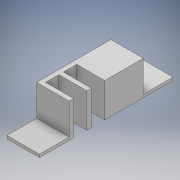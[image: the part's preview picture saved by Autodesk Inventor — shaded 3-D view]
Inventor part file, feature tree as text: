
AUTODESK INVENTOR PART (.ipt)
format: ipt  version: 2017.3 (Build 213256000, 256)  size: 136,704 bytes
history: native  units: mm
features: extrude x3, sketch x3, mirror x1
ambient origin geometry x8: Origin, YZ Plane, XZ Plane, XY Plane, X Axis, Y Axis, Z Axis, Center Point
bodies: Body1 (feature_tree)
feature tree (7):
  extrude  "Extrusion3"  Depth=3.0mm
  extrude  "Extrusion11"  Depth=23.0mm TaperAngle=0.0deg
  mirror  "Mirror1"
  extrude  "Extrusion12"  Depth=2.0mm TaperAngle=0.0deg
  sketch  "Sketch3"  dims[d7=50.0mm d8=3.0mm]
  sketch  "Sketch11"  dims[d9=3.0mm d10=23.0mm d11=0.0mm]
  sketch  "Sketch13"  dims[d46=20.0mm d47=2.0mm d48=0.0mm d57=9.0mm d58=3.0mm d60=2.0mm d61=0.0mm d62=9.0mm]
